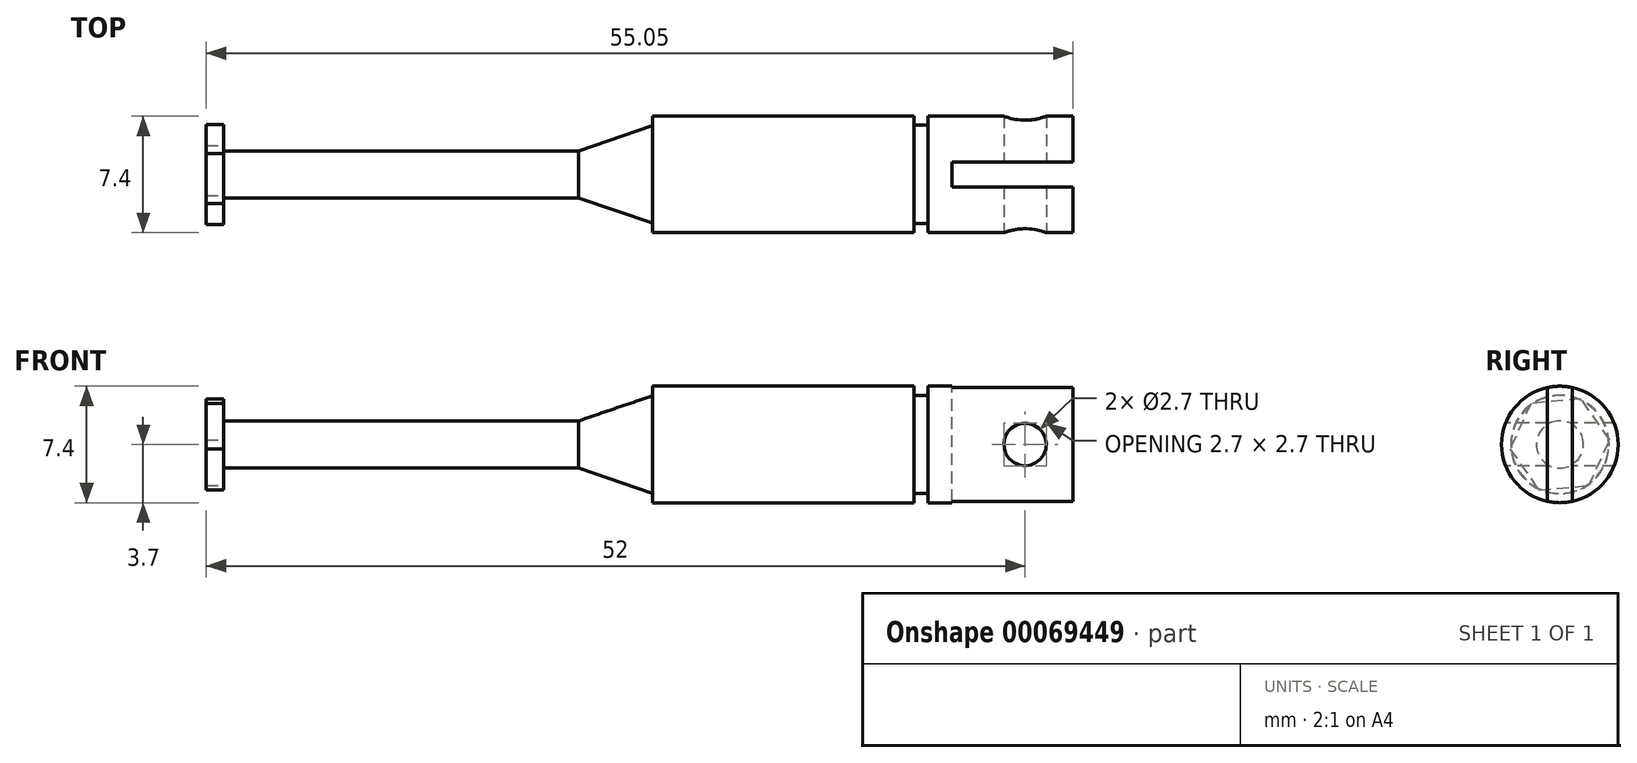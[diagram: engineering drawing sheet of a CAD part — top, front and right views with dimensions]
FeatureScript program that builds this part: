
annotation { "Feature Type Name" : "Feature", "Feature Type Description" : "" }
export const myFeature = defineFeature(function(context is Context, id is Id, definition is map)
    precondition{}
    {
        {
            var Q0;
            Q0=qCreatedBy(makeId("Front.planeOp"),FACE);
            var sketch = newSketch(context, id + "F0", { "sketchPlane" : qUnion([Q0])});
            skLineSegment(sketch, "E0", {"start": v(0, 0) * mm, "end": v(54.5, 0) * mm});
            skLineSegment(sketch, "E1", {"start": v(54.5, 0) * mm, "end": v(54.5, 3.7) * mm});
            skLineSegment(sketch, "E2", {"start": v(27.8, 3.7) * mm, "end": v(27.8, 3.1) * mm});
            skLineSegment(sketch, "E3", {"start": v(27.8, 3.1) * mm, "end": v(23.1, 1.5) * mm});
            skLineSegment(sketch, "E4", {"start": v(23.1, 1.5) * mm, "end": v(0, 1.5) * mm});
            skLineSegment(sketch, "E5", {"start": v(0, 1.5) * mm, "end": v(0, 0) * mm});
            skLineSegment(sketch, "E6.MirrorCS", {"start": v(54.5, 0) * mm, "end": v(54.5, -3.7) * mm});
            skLineSegment(sketch, "E7.MirrorCS", {"start": v(27.8, -3.7) * mm, "end": v(27.8, -3.1) * mm});
            skLineSegment(sketch, "E8.MirrorCS", {"start": v(27.8, -3.1) * mm, "end": v(23.1, -1.5) * mm});
            skLineSegment(sketch, "E9.MirrorCS", {"start": v(23.1, -1.5) * mm, "end": v(0, -1.5) * mm});
            skLineSegment(sketch, "E10.MirrorCS", {"start": v(0, -1.5) * mm, "end": v(0, 0) * mm});
            skLineSegment(sketch, "E11.top", {"start": v(45.3, 3.13) * mm, "end": v(44.4, 3.13) * mm});
            skLineSegment(sketch, "E11.left", {"start": v(44.4, 3.7) * mm, "end": v(44.4, 3.13) * mm});
            skLineSegment(sketch, "E11.right", {"start": v(45.3, 3.7) * mm, "end": v(45.3, 3.13) * mm});
            skLineSegment(sketch, "E12.MirrorCS", {"start": v(44.4, -3.7) * mm, "end": v(44.4, -3.13) * mm});
            skLineSegment(sketch, "E13.MirrorCS", {"start": v(45.3, -3.12) * mm, "end": v(44.4, -3.12) * mm});
            skLineSegment(sketch, "E14.MirrorCS", {"start": v(45.3, -3.7) * mm, "end": v(45.3, -3.13) * mm});
            skLineSegment(sketch, "E15", {"start": v(27.8, 3.7) * mm, "end": v(44.4, 3.7) * mm});
            skLineSegment(sketch, "E16", {"start": v(45.3, 3.7) * mm, "end": v(54.5, 3.7) * mm});
            skLineSegment(sketch, "E17", {"start": v(27.8, -3.7) * mm, "end": v(44.4, -3.7) * mm});
            skLineSegment(sketch, "E18", {"start": v(45.3, -3.7) * mm, "end": v(54.5, -3.7) * mm});
            skSolve(sketch);
        }
        {
            var Q0;
            Q0=makeQuery(id+"F0.imprint","IMPRINT",FACE,{"disambiguationData":[TD([[makeQuery(id+"F0.imprint","IMPRINT",EDGE,{"derivedFrom":sQuery(id+"F0.wireOp",EDGE,"E0")}),1.0]])]});
            var Q1;
            Q1=sQuery(id+"F0.wireOp",EDGE,"E0");
            revolve(context, id + "F1", {"entities" : qUnion([Q0]), "axis" : qUnion([Q1]), "revolveType" : RevolveType.FULL});
        }
        {
            var Q0;
            Q0=makeQuery(id+"F1.opRevolve","SWEPT_FACE",FACE,{"disambiguationData":[OSD([sQuery(id+"F0.wireOp",EDGE,"E1")])]});
            var sketch = newSketch(context, id + "F2", { "sketchPlane" : qUnion([Q0])});
            skLineSegment(sketch, "E19", {"start": v(0, 0) * mm, "end": v(0, 3.7) * mm});
            skLineSegment(sketch, "E20", {"start": v(0, 0) * mm, "end": v(0, -3.7) * mm});
            skLineSegment(sketch, "E21", {"start": v(-0.8, -3.61) * mm, "end": v(-0.8, 3.61) * mm});
            skLineSegment(sketch, "E22.MirrorCS", {"start": v(0.8, -3.61) * mm, "end": v(0.8, 3.61) * mm});
            skSolve(sketch);
        }
        {
            var Q0;
            {var subQ0=sQuery(id+"F2.wireOp",EDGE,"E19");Q0=makeQuery(id+"F2.imprint","IMPRINT",FACE,{"disambiguationData":[TD([[makeQuery(id+"F2.imprint","IMPRINT",EDGE,{"derivedFrom":subQ0}),1.0]])]});}
            var Q1;
            {var subQ0=sQuery(id+"F2.wireOp",EDGE,"E19");Q1=makeQuery(id+"F2.imprint","IMPRINT",FACE,{"disambiguationData":[TD([[makeQuery(id+"F2.imprint","IMPRINT",EDGE,{"derivedFrom":subQ0}),-1.0]])]});}
            extrude(context, id + "F3", {"entities" : qUnion([Q0, Q1]), "operationType" : NewBodyOperationType.REMOVE, "oppositeDirection" : true, "depth" : 7.7 * mm});
        }
        {
            var Q0;
            Q0=qCreatedBy(makeId("Front.planeOp"),FACE);
            var sketch = newSketch(context, id + "F4", { "sketchPlane" : qUnion([Q0])});
            skCircle(sketch, "E23", {"center": v(51.45, 0) * mm, "radius": 1.35 * mm});
            skSolve(sketch);
        }
        {
            var Q0;
            Q0 = qSketchRegion(id + "F4", true);
            extrude(context, id + "F5", {"entities" : qUnion([Q0]), "operationType" : NewBodyOperationType.REMOVE, "endBound" : BoundingType.SYMMETRIC, "oppositeDirection" : true, "depth" : 25 * mm});
        }
        {
            var Q0;
            Q0=makeQuery(id+"F1.opRevolve","SWEPT_FACE",FACE,{"disambiguationData":[OSD([sQuery(id+"F0.wireOp",EDGE,"E5")])]});
            var sketch = newSketch(context, id + "F6", { "sketchPlane" : qUnion([Q0])});
            skCircle(sketch, "E24.cCircle", {"center": v(0, 0) * mm, "radius": 2.76 * mm, "construction": true});
            skLineSegment(sketch, "E24.0", {"start": v(1.84, 2.6) * mm, "end": v(3.18, -0.3) * mm});
            skLineSegment(sketch, "E24.1", {"start": v(3.18, -0.3) * mm, "end": v(1.34, -2.9) * mm});
            skLineSegment(sketch, "E24.2", {"start": v(1.34, -2.9) * mm, "end": v(-1.84, -2.6) * mm});
            skLineSegment(sketch, "E24.3", {"start": v(-1.84, -2.6) * mm, "end": v(-3.18, 0.3) * mm});
            skLineSegment(sketch, "E24.4", {"start": v(-3.18, 0.3) * mm, "end": v(-1.34, 2.9) * mm});
            skLineSegment(sketch, "E24.5", {"start": v(-1.34, 2.9) * mm, "end": v(1.84, 2.6) * mm});
            skPoint(sketch, "E24.0.midPoint", {"position": v(2.5, 1.16) * mm});
            skSolve(sketch);
        }
        {
            var Q0;
            Q0 = qSketchRegion(id + "F6", true);
            extrude(context, id + "F7", {"entities" : qUnion([Q0]), "operationType" : NewBodyOperationType.ADD, "endBound" : BoundingType.SYMMETRIC, "depth" : 1.1 * mm});
        }
    });
